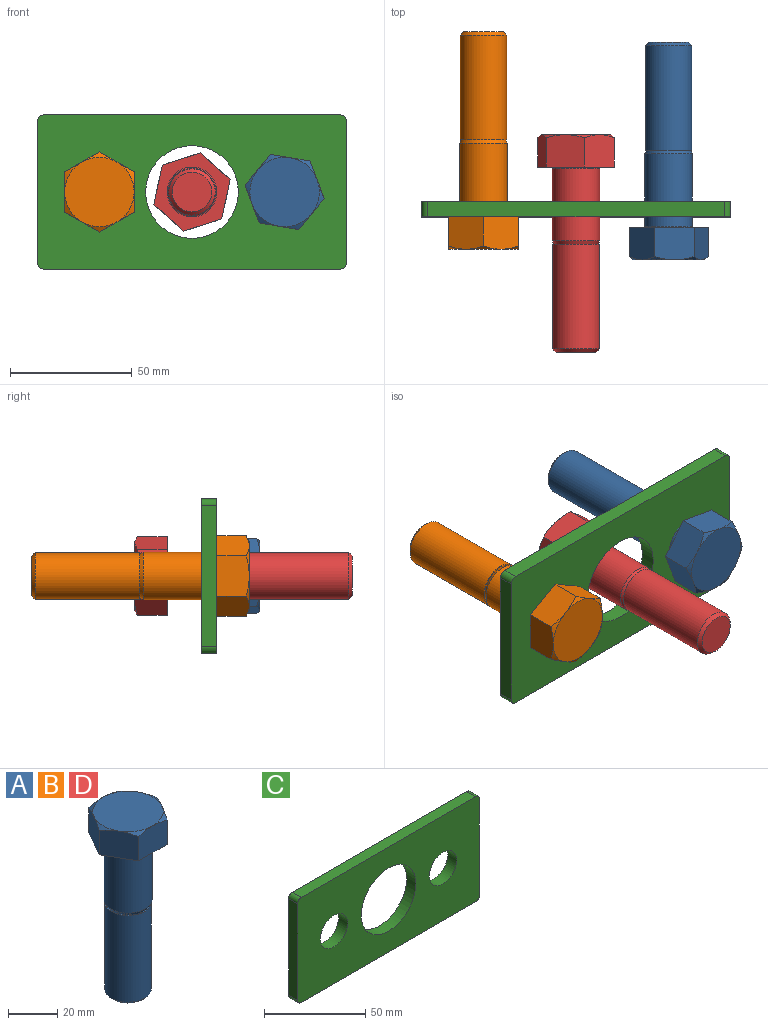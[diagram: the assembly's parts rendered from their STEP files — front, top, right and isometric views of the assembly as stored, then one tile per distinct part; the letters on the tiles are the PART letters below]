
ASSEMBLY  parts=4 mates=4
PART A: 21 faces, bbox 33x33x89.5 mm
  f0: cone r=8.84mm half-angle=45deg, axis (0,0,1), area 108mm2, adj f1,f20
  f1: cylinder r=9.53mm len=43.08mm, axis (0,0,-1), area 2577.9mm2, adj f0,f19
  f2: cone r=9.39mm half-angle=27.9deg, axis (0,0,1), area 91.8mm2, adj f3,f19
  f3: cylinder r=9.75mm len=29.88mm, axis (0,0,-1), area 1830.9mm2, adj f2,f4
  f4: torus R=10.25mm, axis (0,0,-1), area 49mm2, adj f3,f18
  f5: plane 14.29x13.31mm, normal (-0.87,0.5,0), area 212.4mm2, adj f6,f10,f15,f16,f17,f18
  f6: plane 16.5x13.31mm, normal (0,1,0), area 212.4mm2, adj f5,f7,f14,f16,f17,f18
  f7: plane 14.29x13.31mm, normal (0.87,0.5,0), area 212.4mm2, adj f6,f9,f12,f14,f16,f18
  f8: plane 16.5x13.31mm, normal (0,-1,0), area 212.4mm2, adj f9,f10,f11,f13,f16,f18
  f9: plane 14.29x13.31mm, normal (0.87,-0.5,0), area 212.4mm2, adj f7,f8,f11,f12,f16,f18
  f10: plane 14.29x13.31mm, normal (-0.87,-0.5,0), area 212.4mm2, adj f5,f8,f13,f15,f16,f18
  f11: cone r=15.39mm half-angle=60deg, axis (0,0,-1), area 12.7mm2, adj f8,f9,f16
  f12: cone r=15.39mm half-angle=60deg, axis (0,0,-1), area 12.7mm2, adj f7,f9,f16
  f13: cone r=15.39mm half-angle=60deg, axis (0,0,-1), area 12.7mm2, adj f8,f10,f16
  f14: cone r=15.39mm half-angle=60deg, axis (0,0,-1), area 12.7mm2, adj f6,f7,f16
  f15: cone r=15.39mm half-angle=60deg, axis (0,0,-1), area 12.7mm2, adj f5,f10,f16
  f16: plane 28.58x28.57mm, normal (0,0,1), area 641.3mm2, adj f5,f6,f7,f8,f9,f10,f11,f12
  f17: cone r=15.39mm half-angle=60deg, axis (0,0,-1), area 12.7mm2, adj f5,f6,f16
  f18: plane 32.99x28.57mm, normal (0,0,-1), area 376.8mm2, adj f4,f5,f6,f7,f8,f9,f10
  f19: plane 19.05x19.05mm, normal (0,0,1), area 29.1mm2, adj f1,f2
  f20: plane 16.3x16.3mm, normal (0,0,-1), area 208.7mm2, adj f0
PART B: same geometry as A
PART C: 13 faces, bbox 127x6.4x63.5 mm
  f0: plane 58.42x6.35mm, normal (1,0,0), area 371mm2, adj f1,f10,f11,f12
  f1: cylinder r=2.54mm len=6.35mm, axis (0,1,0), area 25.3mm2, adj f0,f2,f11,f12
  f2: plane 121.92x6.35mm, normal (0,0,1), area 774.2mm2, adj f1,f3,f11,f12
  f3: cylinder r=2.54mm len=6.35mm, axis (0,1,0), area 25.3mm2, adj f2,f4,f11,f12
  f4: plane 58.42x6.35mm, normal (-1,0,0), area 371mm2, adj f3,f5,f11,f12
  f5: cylinder r=2.54mm len=6.35mm, axis (0,1,0), area 25.3mm2, adj f4,f6,f11,f12
  f6: plane 121.92x6.35mm, normal (0,0,-1), area 774.2mm2, adj f5,f10,f11,f12
  f7: cylinder r=19.05mm len=38.1mm, axis (0,1,0), area 760.1mm2, adj f11,f12
  f8: cylinder r=9.53mm len=19.05mm, axis (0,1,0), area 380mm2, adj f11,f12
  f9: cylinder r=9.53mm len=19.05mm, axis (0,1,0), area 380mm2, adj f11,f12
  f10: cylinder r=2.54mm len=6.35mm, axis (0,1,0), area 25.3mm2, adj f0,f6,f11,f12
  f11: plane 127x63.5mm, normal (0,-1,0), area 6348.8mm2, adj f0,f1,f2,f3,f4,f5,f6,f7
  f12: plane 127x63.5mm, normal (0,1,0), area 6348.8mm2, adj f0,f1,f2,f3,f4,f5,f6,f7
PART D: same geometry as A
PLACE A rot(axis=(0.99,0.08,-0.08),90.4deg) t=(39.15,-7.16,-0.38)mm
PLACE B rot(axis=(0.58,0.58,-0.58),120deg) t=(-37.05,-2.82,-0.38)mm
PLACE C t=(1.05,3.53,-0.38)mm fixed
PLACE D rot(axis=(-0.98,-0.15,-0.15),91.4deg) t=(1.05,17.69,-0.38)mm
MATE cylindrical A.f4 <-> C.f9  axis (0,1,0) through (39.15,23.22,-0.38)mm
MATE cylindrical B.f4 <-> C.f8  axis (0,1,0) through (-37.05,12.62,-0.38)mm
MATE planar B.f18 <-> C.f7  axis (0,1,0) through (-51.34,-2.82,7.87)mm
MATE cylindrical D.f4 <-> C.f7  axis (0,-1,0) through (1.05,2.25,-0.38)mm
